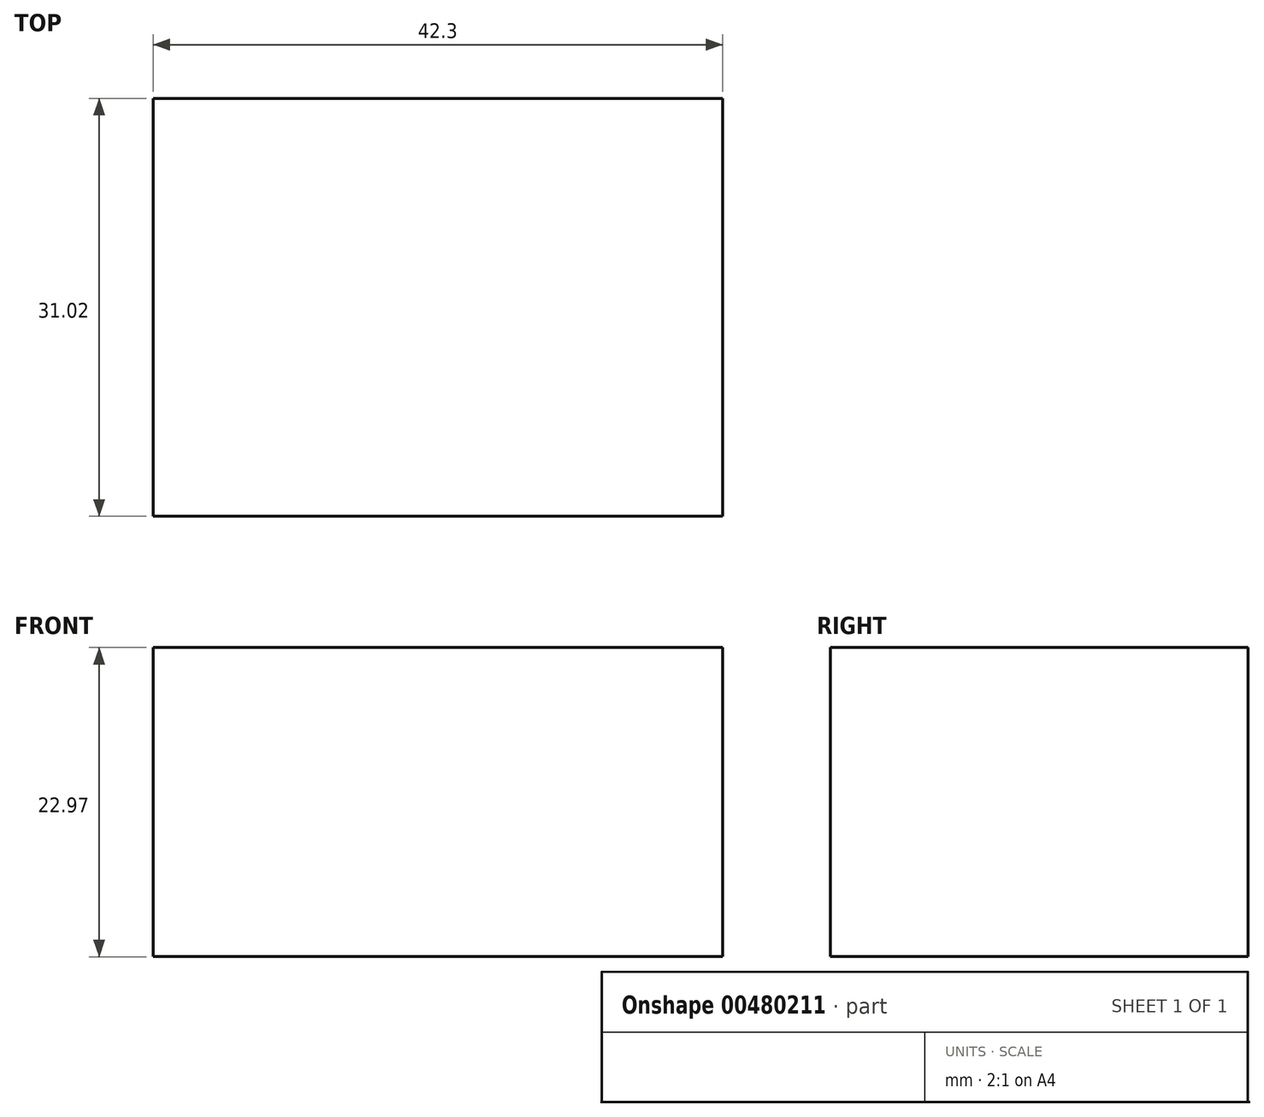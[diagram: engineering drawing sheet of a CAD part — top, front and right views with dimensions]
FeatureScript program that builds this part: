
annotation { "Feature Type Name" : "Feature", "Feature Type Description" : "" }
export const myFeature = defineFeature(function(context is Context, id is Id, definition is map)
    precondition{}
    {
        {
            var Q0;
            Q0=qCreatedBy(makeId("Right.planeOp"),FACE);
            var sketch = newSketch(context, id + "F0", { "sketchPlane" : qUnion([Q0])});
            skLineSegment(sketch, "E0.bottom", {"start": v(-4.64, -15.38) * mm, "end": v(-35.66, -15.38) * mm});
            skLineSegment(sketch, "E0.top", {"start": v(-4.64, 7.6) * mm, "end": v(-35.66, 7.6) * mm});
            skLineSegment(sketch, "E0.left", {"start": v(-4.64, -15.38) * mm, "end": v(-4.64, 7.6) * mm});
            skLineSegment(sketch, "E0.right", {"start": v(-35.66, -15.38) * mm, "end": v(-35.66, 7.6) * mm});
            skSolve(sketch);
        }
        {
            var Q0;
            Q0 = qSketchRegion(id + "F0", true);
            extrude(context, id + "F1", {"entities" : qUnion([Q0]), "depth" : 42.3 * mm});
        }
    });
